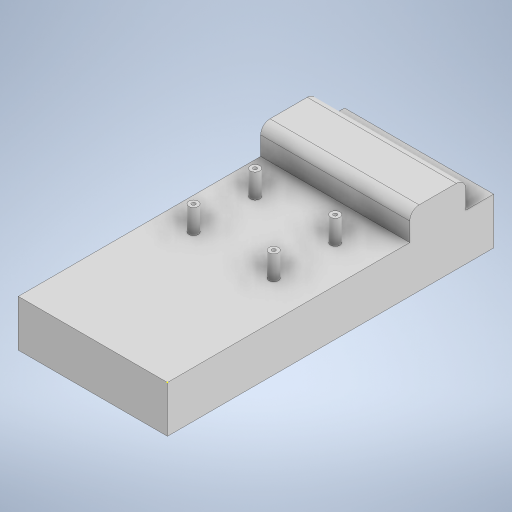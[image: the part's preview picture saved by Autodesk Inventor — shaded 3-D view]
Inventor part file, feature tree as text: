
AUTODESK INVENTOR PART (.ipt)
format: ipt  version: 2024.2 (Build 282272000, 272)  size: 280,064 bytes
history: native  units: mm
features: sketch x5, extrude x4, fillet x1
ambient origin geometry x8: Origin, YZ Plane, XZ Plane, XY Plane, X Axis, Y Axis, Z Axis, Center Point
bodies: Solid1 (feature_tree)
feature tree (10):
  extrude  "Extrusion1"  Depth=175.0mm
  sketch  "Sketch2"  dims[d2=25.0mm d3=0.0mm d4=15.0mm d5=15.0mm]
  extrude  "Extrusion2"  Depth=15.0mm
  fillet  "Fillet1"  Radius=15.0mm
  extrude  "Extrusion3"  Depth=80.0mm TaperAngle=0.0deg
  extrude  "Extrusion4"  Depth=5.0mm
  sketch  "Sketch1"  dims[d0=80.0mm d1=175.0mm]
  sketch  "Sketch3"  dims[d6=30.0mm d7=80.0mm d8=0.0mm]
  sketch  "Sketch4"  dims[d9=5.0mm d10=5.0mm]
  sketch  "Sketch5"  dims[d11=5.0mm d12=5.0mm d13=5.0mm d14=20.0mm d15=20.0mm d16=43.0mm d17=43.0mm d18=20.0mm d19=20.0mm d20=33.0mm d21=33.0mm d22=13.0mm d23=0.0mm d24=2.0mm d25=2.0mm d26=2.0mm d27=2.0mm d28=13.0mm d29=0.0mm]
